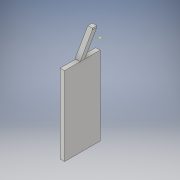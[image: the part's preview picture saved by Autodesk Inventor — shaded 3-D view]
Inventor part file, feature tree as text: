
AUTODESK INVENTOR PART (.ipt)
format: ipt  version: 2017 (Build 210142000, 142)  size: 153,088 bytes
history: native  units: in
note: dims shown in document units (in); Inventor stores cm internally (conversion verified against a paired STEP export)
features: sketch x9, extrude x7, projected_geometry x1
ambient origin geometry x8: Origin, YZ Plane, XZ Plane, XY Plane, X Axis, Y Axis, Z Axis, Center Point
bodies: Solid1 (feature_tree)
feature tree (17):
  extrude  "Extrusion1"  Depth=0.125in
  sketch  "Sketch2"  dims[d2=1.0in d3=0.0in d7=0.125in d8=0.0in]
  extrude  "Extrusion2"  Depth=0.125in TaperAngle=0.0deg
  extrude  "Extrusion3"  Depth=0.125in TaperAngle=0.0deg
  sketch  "Sketch5"  dims[d17=0.4375in d18=0.0in]
  extrude  "Extrusion4"  Depth=0.4375in TaperAngle=0.0deg
  extrude  "Extrusion5"  [1 undecoded]
  extrude  "Extrusion6"  [1 undecoded]
  extrude  "Extrusion7"  [1 undecoded]
  sketch  "Sketch1"  dims[d0=2.21in d1=0.125in]
  projected_geometry  "Projected Loop1"
  sketch  "Sketch3"  dims[d9=1.0in d10=0.0in d11=0.125in d12=0.0in]
  sketch  "Sketch4"  dims[d13=1.0in d14=0.0in d15=0.4375in d16=0.0in]
  sketch  "Sketch6"
  sketch  "Sketch7"
  sketch  "Sketch8"
  sketch  "Sketch9"
note: 3 required parameter values undecoded (feature->parameter linkage not recoverable at this tier; creation-order binding heuristic only, values carry confidence <= 0.55)
